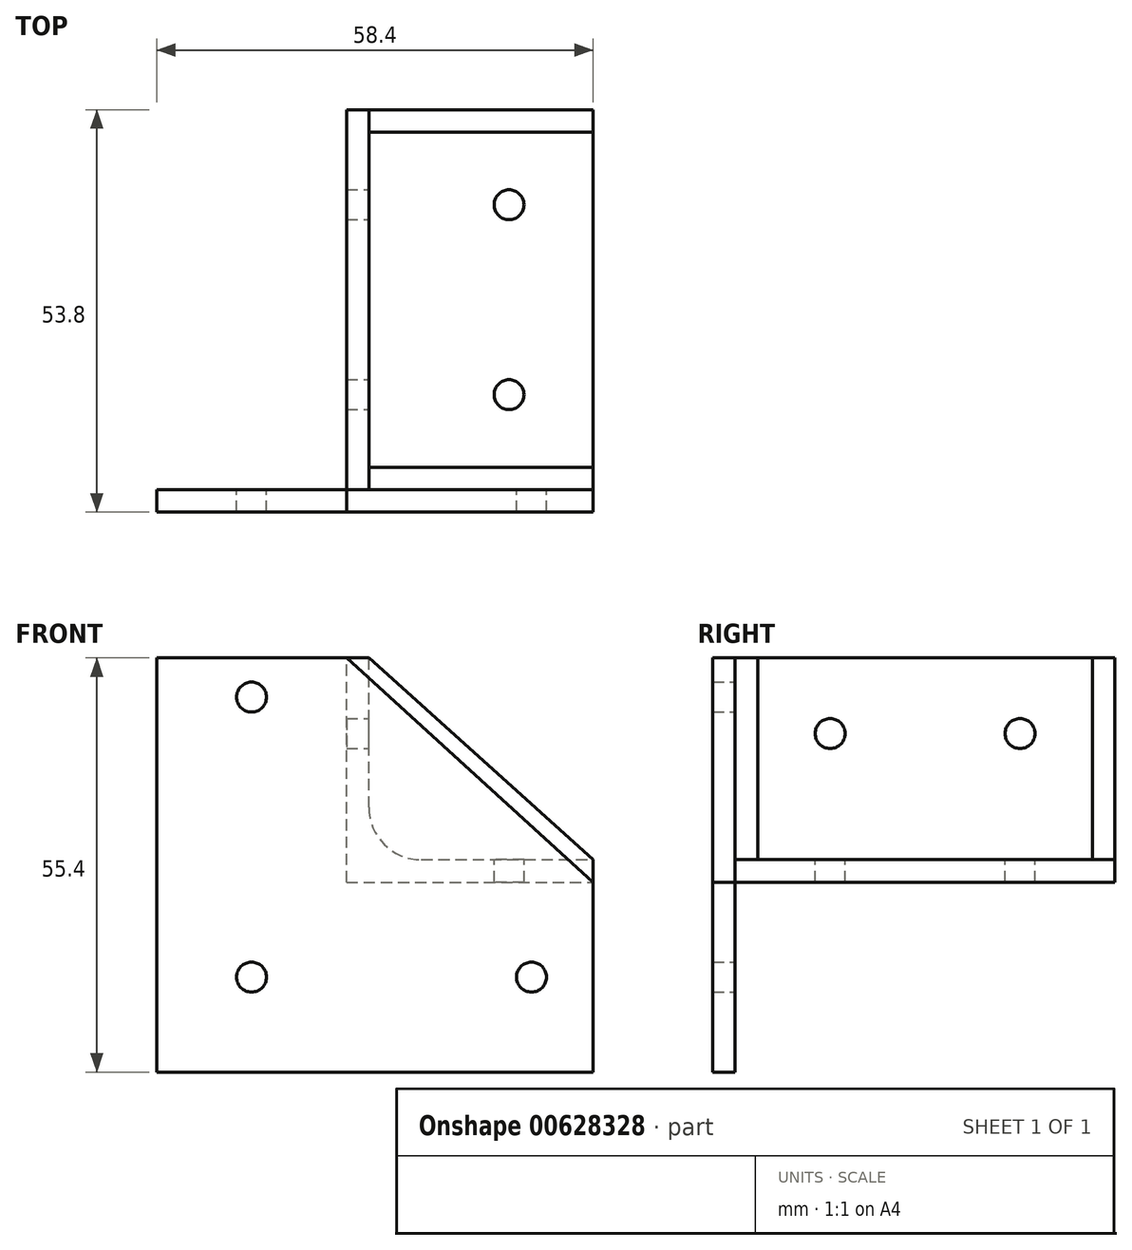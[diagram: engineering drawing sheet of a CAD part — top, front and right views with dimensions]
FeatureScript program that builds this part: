
annotation { "Feature Type Name" : "Feature", "Feature Type Description" : "" }
export const myFeature = defineFeature(function(context is Context, id is Id, definition is map)
    precondition{}
    {
        {
            var Q0;
            Q0=qCreatedBy(makeId("Front.planeOp"),FACE);
            var sketch = newSketch(context, id + "F0", { "sketchPlane" : qUnion([Q0])});
            skLineSegment(sketch, "E0.bottom", {"start": v(0, 0) * mm, "end": v(30, 0) * mm});
            skLineSegment(sketch, "E0.top", {"start": v(0, 3) * mm, "end": v(30, 3) * mm});
            skLineSegment(sketch, "E0.left", {"start": v(0, 0) * mm, "end": v(0, 3) * mm});
            skLineSegment(sketch, "E0.right", {"start": v(30, 0) * mm, "end": v(30, 3) * mm});
            skLineSegment(sketch, "E1.bottom", {"start": v(0, 0) * mm, "end": v(-3, 0) * mm});
            skLineSegment(sketch, "E1.top", {"start": v(0, 30) * mm, "end": v(-3, 30) * mm});
            skLineSegment(sketch, "E1.left", {"start": v(0, 0) * mm, "end": v(0, 30) * mm});
            skLineSegment(sketch, "E1.right", {"start": v(-3, 0) * mm, "end": v(-3, 30) * mm});
            skSolve(sketch);
        }
        {
            var Q0;
            Q0 = qSketchRegion(id + "F0", true);
            extrude(context, id + "F1", {"entities" : qUnion([Q0]), "depth" : 50.8 * mm, "offsetDistance" : 25 * mm});
        }
        {
            var Q0;
            Q0=makeQuery(id+"F1.opExtrude","SWEPT_FACE",FACE,{"disambiguationData":[OSD([sQuery(id+"F0.wireOp",EDGE,"E0.top")])]});
            var sketch = newSketch(context, id + "F2", { "sketchPlane" : qUnion([Q0])});
            skLineSegment(sketch, "E2", {"start": v(15, 0) * mm, "end": v(15, -50.8) * mm, "construction": true});
            skLineSegment(sketch, "E3", {"start": v(15, -25.4) * mm, "end": v(30, -25.4) * mm, "construction": true});
            skLineSegment(sketch, "E4", {"start": v(22.5, -25.4) * mm, "end": v(22.5, 0) * mm, "construction": true});
            skLineSegment(sketch, "E5", {"start": v(22.5, -12.7) * mm, "end": v(15, -12.7) * mm, "construction": true});
            skLineSegment(sketch, "E6", {"start": v(18.75, -12.7) * mm, "end": v(18.75, 0) * mm, "construction": true});
            skCircle(sketch, "E7", {"center": v(18.75, -12.7) * mm, "radius": 2 * mm});
            skCircle(sketch, "E8.MirrorC", {"center": v(18.75, -38.1) * mm, "radius": 2 * mm});
            skSolve(sketch);
        }
        {
            var Q0;
            Q0 = qSketchRegion(id + "F2", true);
            extrude(context, id + "F3", {"entities" : qUnion([Q0]), "operationType" : NewBodyOperationType.REMOVE, "endBound" : BoundingType.THROUGH_ALL, "oppositeDirection" : true, "depth" : 25 * mm, "offsetDistance" : 25 * mm});
        }
        {
            var Q0;
            Q0=makeQuery(id+"F1.opExtrude","SWEPT_FACE",FACE,{"disambiguationData":[OSD([sQuery(id+"F0.wireOp",EDGE,"E1.left")])]});
            var sketch = newSketch(context, id + "F4", { "sketchPlane" : qUnion([Q0])});
            skLineSegment(sketch, "E9", {"start": v(-50.8, 16.5) * mm, "end": v(0, 16.5) * mm, "construction": true});
            skLineSegment(sketch, "E10", {"start": v(-25.4, 16.5) * mm, "end": v(-25.4, 30) * mm, "construction": true});
            skLineSegment(sketch, "E11", {"start": v(-25.4, 23.25) * mm, "end": v(-50.8, 23.25) * mm, "construction": true});
            skLineSegment(sketch, "E12", {"start": v(-38.1, 23.25) * mm, "end": v(-38.1, 16.5) * mm, "construction": true});
            skCircle(sketch, "E13", {"center": v(-38.1, 19.87) * mm, "radius": 2 * mm});
            skCircle(sketch, "E14.MirrorC", {"center": v(-12.7, 19.88) * mm, "radius": 2 * mm});
            skSolve(sketch);
        }
        {
            var Q0;
            Q0 = qSketchRegion(id + "F4", true);
            extrude(context, id + "F5", {"entities" : qUnion([Q0]), "operationType" : NewBodyOperationType.REMOVE, "endBound" : BoundingType.THROUGH_ALL, "oppositeDirection" : true, "depth" : 25 * mm, "offsetDistance" : 25 * mm});
        }
        {
            var Q0;
            Q0=makeQuery(id+"F1.opExtrude","CAP_FACE",FACE,{"disambiguationData":[OSD([sQuery(id+"F0.wireOp",EDGE,"E0.bottom"),sQuery(id+"F0.wireOp",EDGE,"E0.top"),sQuery(id+"F0.wireOp",EDGE,"E0.right"),sQuery(id+"F0.wireOp",EDGE,"E1.bottom"),sQuery(id+"F0.wireOp",EDGE,"E1.top"),sQuery(id+"F0.wireOp",EDGE,"E1.left"),sQuery(id+"F0.wireOp",EDGE,"E1.right")])],"isStart":false});
            var sketch = newSketch(context, id + "F6", { "sketchPlane" : qUnion([Q0])});
            skLineSegment(sketch, "E15", {"start": v(0, 30) * mm, "end": v(30, 3) * mm});
            skLineSegment(sketch, "E16", {"start": v(30, 3) * mm, "end": v(0, 3) * mm});
            skLineSegment(sketch, "E17", {"start": v(0, 3) * mm, "end": v(0, 30) * mm});
            skSolve(sketch);
        }
        {
            var Q0;
            Q0 = qSketchRegion(id + "F6", true);
            extrude(context, id + "F7", {"entities" : qUnion([Q0]), "operationType" : NewBodyOperationType.ADD, "oppositeDirection" : true, "depth" : 3 * mm, "offsetDistance" : 25 * mm});
        }
        {
            var Q0;
            Q0=makeQuery(id+"F1.opExtrude","CAP_FACE",FACE,{"disambiguationData":[OSD([sQuery(id+"F0.wireOp",EDGE,"E0.bottom"),sQuery(id+"F0.wireOp",EDGE,"E0.top"),sQuery(id+"F0.wireOp",EDGE,"E0.right"),sQuery(id+"F0.wireOp",EDGE,"E1.bottom"),sQuery(id+"F0.wireOp",EDGE,"E1.top"),sQuery(id+"F0.wireOp",EDGE,"E1.left"),sQuery(id+"F0.wireOp",EDGE,"E1.right")])],"isStart":true});
            var sketch = newSketch(context, id + "F8", { "sketchPlane" : qUnion([Q0])});
            skLineSegment(sketch, "E18", {"start": v(-30, 3) * mm, "end": v(0, 30) * mm});
            skLineSegment(sketch, "E19", {"start": v(0, 30) * mm, "end": v(0, 3) * mm});
            skLineSegment(sketch, "E20", {"start": v(0, 3) * mm, "end": v(-30, 3) * mm});
            skSolve(sketch);
        }
        {
            var Q0;
            Q0 = qSketchRegion(id + "F8", true);
            extrude(context, id + "F9", {"entities" : qUnion([Q0]), "operationType" : NewBodyOperationType.ADD, "oppositeDirection" : true, "depth" : 3 * mm, "offsetDistance" : 25 * mm});
        }
        {
            var Q0;
            Q0=makeQuery(id+"F1.opExtrude","SWEPT_EDGE",EDGE,{"disambiguationData":[OSD([sQuery(id+"F0.wireOp",EDGE,"E0.top"),sQuery(id+"F0.wireOp",EDGE,"E1.left")])]});
            fillet(context, id + "F10", {"entities" : qUnion([Q0]), "radius" : 7 * mm, "tangentPropagation" : true, "allowEdgeOverflow" : false});
        }
        {
            var Q0;
            Q0=makeQuery(id+"F7.boolean.opBoolean","MERGE",FACE,{"derivedFrom":[makeQuery(id+"F1.opExtrude","CAP_FACE",FACE,{"disambiguationData":[OSD([sQuery(id+"F0.wireOp",EDGE,"E0.bottom"),sQuery(id+"F0.wireOp",EDGE,"E0.top"),sQuery(id+"F0.wireOp",EDGE,"E0.right"),sQuery(id+"F0.wireOp",EDGE,"E1.bottom"),sQuery(id+"F0.wireOp",EDGE,"E1.top"),sQuery(id+"F0.wireOp",EDGE,"E1.left"),sQuery(id+"F0.wireOp",EDGE,"E1.right")])],"isStart":false}),makeQuery(id+"F7.opExtrude","CAP_FACE",FACE,{"disambiguationData":[OSD([sQuery(id+"F6.wireOp",EDGE,"E15"),sQuery(id+"F6.wireOp",EDGE,"E16"),sQuery(id+"F6.wireOp",EDGE,"E17")])],"isStart":true})]});
            var sketch = newSketch(context, id + "F11", { "sketchPlane" : qUnion([Q0])});
            skLineSegment(sketch, "E21.bottom", {"start": v(-3, 0) * mm, "end": v(-28.4, 0) * mm, "construction": true});
            skLineSegment(sketch, "E21.top", {"start": v(-3, 80.45) * mm, "end": v(-28.4, 80.45) * mm, "construction": true});
            skLineSegment(sketch, "E21.left", {"start": v(-3, 0) * mm, "end": v(-3, 80.45) * mm, "construction": true});
            skLineSegment(sketch, "E21.right", {"start": v(-28.4, 0) * mm, "end": v(-28.4, 80.45) * mm, "construction": true});
            skLineSegment(sketch, "E22.bottom", {"start": v(-28.4, 0) * mm, "end": v(123.14, 0) * mm, "construction": true});
            skLineSegment(sketch, "E22.top", {"start": v(-28.4, -25.4) * mm, "end": v(123.14, -25.4) * mm, "construction": true});
            skLineSegment(sketch, "E22.left", {"start": v(-28.4, 0) * mm, "end": v(-28.4, -25.4) * mm, "construction": true});
            skLineSegment(sketch, "E22.right", {"start": v(123.14, 0) * mm, "end": v(123.14, -25.4) * mm, "construction": true});
            skLineSegment(sketch, "E23.bottom", {"start": v(-3, 30) * mm, "end": v(-28.4, 30) * mm});
            skLineSegment(sketch, "E23.top", {"start": v(-3, -25.4) * mm, "end": v(-28.4, -25.4) * mm});
            skLineSegment(sketch, "E23.left", {"start": v(-3, 30) * mm, "end": v(-3, -25.4) * mm});
            skLineSegment(sketch, "E23.right", {"start": v(-28.4, 30) * mm, "end": v(-28.4, -25.4) * mm});
            skLineSegment(sketch, "E24.bottom", {"start": v(-28.4, -25.4) * mm, "end": v(30, -25.4) * mm});
            skLineSegment(sketch, "E24.top", {"start": v(-28.4, 0) * mm, "end": v(30, 0) * mm});
            skLineSegment(sketch, "E24.left", {"start": v(-28.4, -25.4) * mm, "end": v(-28.4, 0) * mm});
            skLineSegment(sketch, "E24.right", {"start": v(30, -25.4) * mm, "end": v(30, 0) * mm});
            skLineSegment(sketch, "E25", {"start": v(-3, 30) * mm, "end": v(30, 0) * mm});
            skLineSegment(sketch, "E26", {"start": v(30, -12.7) * mm, "end": v(13.5, -12.7) * mm, "construction": true});
            skLineSegment(sketch, "E27", {"start": v(13.5, -12.7) * mm, "end": v(13.5, -25.4) * mm, "construction": true});
            skPoint(sketch, "E28.orphan", {"position": v(-3, -12.7) * mm});
            skPoint(sketch, "E29.start.orphan", {"position": v(13.5, -19.05) * mm});
            skCircle(sketch, "E30", {"center": v(21.75, -12.7) * mm, "radius": 2 * mm});
            skLineSegment(sketch, "E31", {"start": v(-28.4, -25.4) * mm, "end": v(-3, 0) * mm, "construction": true});
            skCircle(sketch, "E32.MirrorC", {"center": v(-15.7, 24.75) * mm, "radius": 2 * mm});
            skCircle(sketch, "E33", {"center": v(-15.7, -12.7) * mm, "radius": 2 * mm});
            skSolve(sketch);
        }
        {
            var Q0;
            Q0 = qSketchRegion(id + "F11", true);
            extrude(context, id + "F12", {"entities" : qUnion([Q0]), "depth" : 3 * mm, "offsetDistance" : 25 * mm});
        }
    });
